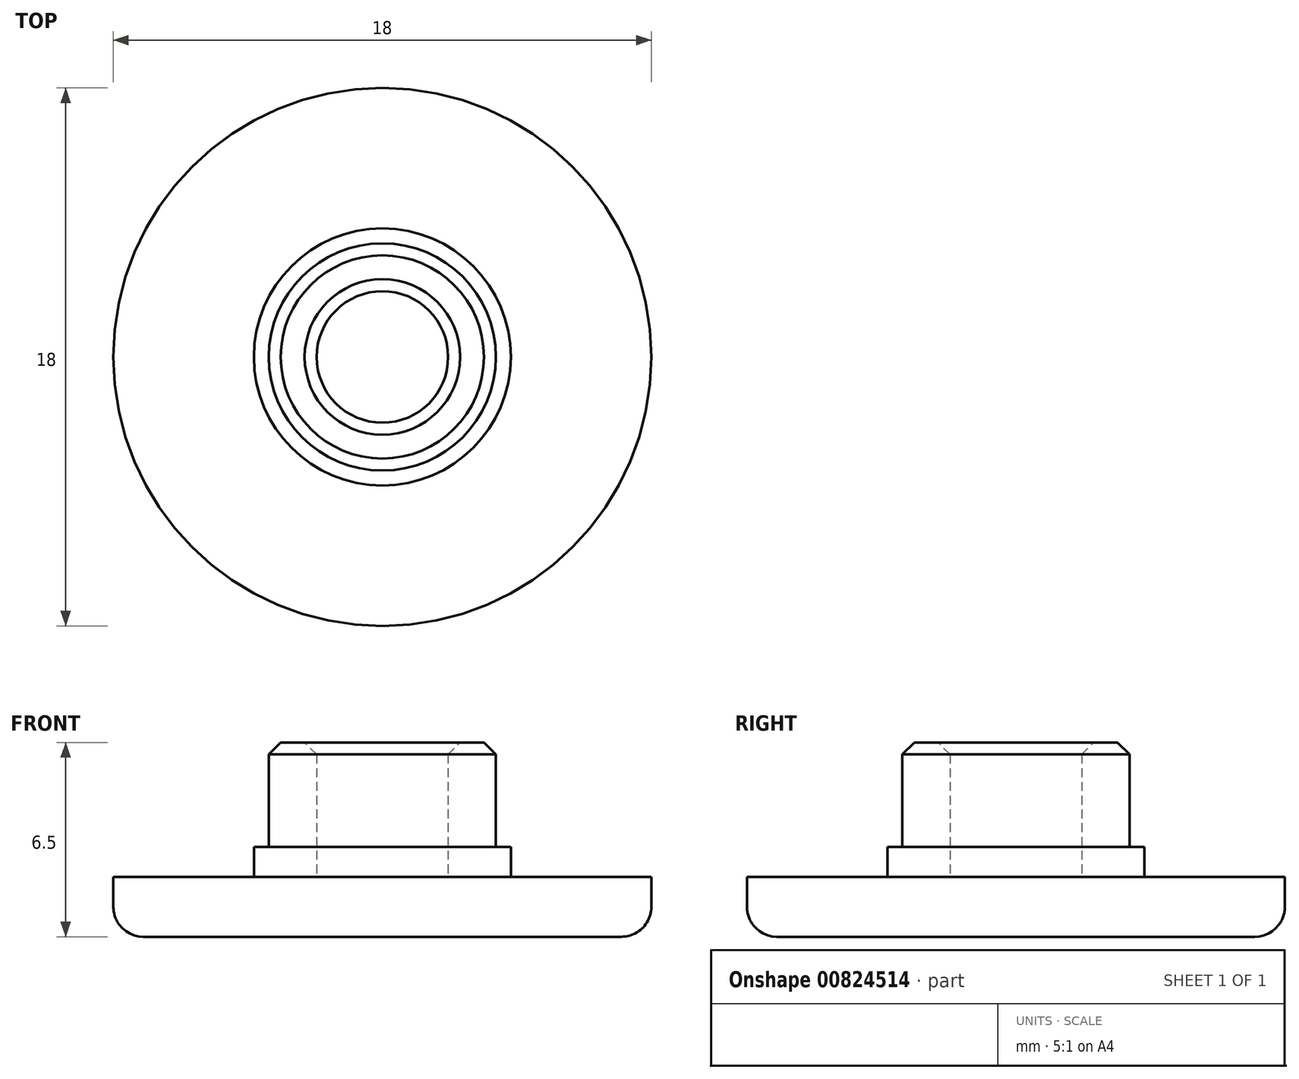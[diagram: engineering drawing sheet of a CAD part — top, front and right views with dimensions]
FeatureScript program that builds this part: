
annotation { "Feature Type Name" : "Feature", "Feature Type Description" : "" }
export const myFeature = defineFeature(function(context is Context, id is Id, definition is map)
    precondition{}
    {
        {
            var Q0;
            Q0=qCreatedBy(makeId("Top.planeOp"),FACE);
            var sketch = newSketch(context, id + "F0", { "sketchPlane" : qUnion([Q0])});
            skCircle(sketch, "E0", {"center": v(0, 0) * mm, "radius": 3.8 * mm});
            skCircle(sketch, "E1", {"center": v(0, 0) * mm, "radius": 4.3 * mm});
            skCircle(sketch, "E2", {"center": v(0, 0) * mm, "radius": 9 * mm});
            skCircle(sketch, "E3", {"center": v(0, 0) * mm, "radius": 2.2 * mm});
            skSolve(sketch);
        }
        {
            var Q0;
            Q0 = qSketchRegion(id + "F0", true);
            var Q1;
            Q1=makeQuery(id+"F0.imprint","IMPRINT",FACE,{"disambiguationData":[TD([[makeQuery(id+"F0.imprint","IMPRINT",EDGE,{"derivedFrom":sQuery(id+"F0.wireOp",EDGE,"E3")}),1.0]])]});
            extrude(context, id + "F1", {"entities" : qUnion([Q0, Q1]), "depth" : 2 * mm, "offsetDistance" : 25 * mm});
        }
        {
            var Q0;
            Q0=makeQuery(id+"F0.imprint","IMPRINT",FACE,{"disambiguationData":[TD([[makeQuery(id+"F0.imprint","IMPRINT",EDGE,{"derivedFrom":sQuery(id+"F0.wireOp",EDGE,"E0")}),-1.0]])]});
            extrude(context, id + "F2", {"entities" : qUnion([Q0]), "operationType" : NewBodyOperationType.ADD, "depth" : 3 * mm, "offsetDistance" : 25 * mm});
        }
        {
            var Q0;
            Q0=makeQuery(id+"F0.imprint","IMPRINT",FACE,{"disambiguationData":[TD([[makeQuery(id+"F0.imprint","IMPRINT",EDGE,{"derivedFrom":sQuery(id+"F0.wireOp",EDGE,"E0")}),1.0]])]});
            extrude(context, id + "F3", {"entities" : qUnion([Q0]), "operationType" : NewBodyOperationType.ADD, "depth" : 6.5 * mm, "offsetDistance" : 25 * mm});
        }
        {
            var Q0;
            Q0=makeQuery(id+"F1.opExtrude","CAP_EDGE",EDGE,{"disambiguationData":[OSD([sQuery(id+"F0.wireOp",EDGE,"E2")])],"isStart":true});
            fillet(context, id + "F4", {"entities" : qUnion([Q0]), "radius" : 1 * mm, "tangentPropagation" : true, "allowEdgeOverflow" : false});
        }
        {
            var Q0;
            Q0=makeQuery(id+"F3.opExtrude","CAP_EDGE",EDGE,{"disambiguationData":[OSD([sQuery(id+"F0.wireOp",EDGE,"E0")])],"isStart":false});
            var Q1;
            Q1=makeQuery(id+"F3.opExtrude","CAP_EDGE",EDGE,{"disambiguationData":[OSD([sQuery(id+"F0.wireOp",EDGE,"E3")])],"isStart":false});
            chamfer(context, id + "F5", {"entities" : qUnion([Q0, Q1]), "width" : 0.4 * mm, "tangentPropagation" : true});
        }
    });
